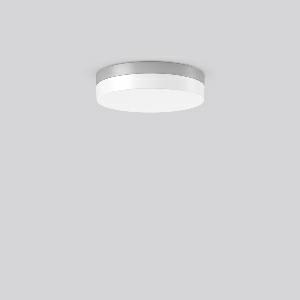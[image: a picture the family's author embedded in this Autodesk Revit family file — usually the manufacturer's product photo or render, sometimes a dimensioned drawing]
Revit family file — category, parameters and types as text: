
# Revit family: flat_slim_round_312630_004_1_19_6174
name_source: partatom
category: Lighting Fixtures
units: mm (PartAtom-declared; Revit-internal decimal feet)

## family parameters
Cut with Voids When Loaded = No
Host = Face
Light Source = No
Part Type = Normal
Room Calculation Point = No
Round Connector Dimension = Use Diameter
Shared = No

## types (1)
- MultiLumen 1 830 (1 x LED Modul 830, 1450 lm, 3000)
    Apparent Load = 11 VA
    CIE Flux Codes = 38 68 88 84 100
    Color Rendering = 80
    Color Temperature = 3000
    Default Elevation = 1800 mm
    Height = 70 mm
    Lamp = 1 x LED Modul 830
    Lamp Light Flux = 1450 lm
    Lamp count = 1
    Length = 300 mm
    Lifetime = 50000 h
    Luminous efficacy = 132 lm/W
    Manufacturer = RZB
    ModVariant = No
    Model = 312630.004.1.19
    Mounting Place = Ceiling
    Mounting Type = Surface mounted
    Number of Poles = 1
    OnlyDefault = Yes
    Power Factor = 1
    Product Name = FLAT SLIM round
    Product group = Surface mounted ceiling and wall luminaires
    ProductGroupID = 305
    Protection Class = Protection class I
    Protection Degree = Degree of protection
    RLX_Detail_Level = 1
    RLX_Emergency_Light_Flux = 0 lm
    RLX_Emergency_Type = 0
    RLX_Emergency_Type_DB = No
    RlxData = <blob elided: 17381 chars, md5=9c68661e>
    Socket = socket
    Standby Power = 0 W
    System Light Flux = 1450 lm
    System Power = 11 W
    Type Comments = MultiLumen 1 830
    Type Image = 312629.004.jpg
    URL = http://relux.com
    VarID = multilumen_1_830
    Voltage = 0 V
    Weight = 0.00 kg
    Width = 0 mm  [stored 0 ft]

note: [stored X ft] marks values corroborated as IEEE doubles in the binary element streams (Revit-internal decimal feet)

## geometry (parser evidence)
native form markers: Blend x4, Sweep x15
no freeform markers — native parametric forms only
